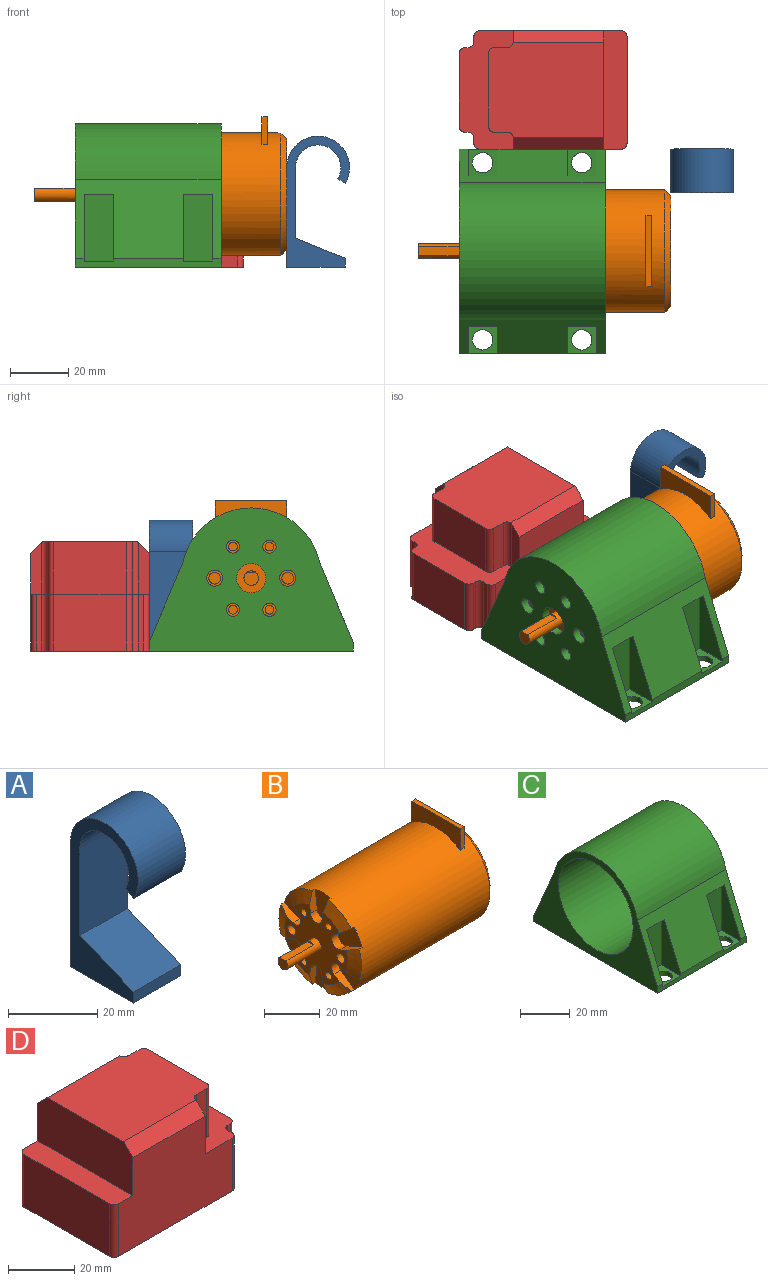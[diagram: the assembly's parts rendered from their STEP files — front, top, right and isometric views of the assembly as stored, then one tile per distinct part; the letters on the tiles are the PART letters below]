
ASSEMBLY  parts=4 mates=11
PART A: 10 faces, bbox 15x21.5x44.9 mm
  f0: cylinder r=7.76mm len=15.53mm, axis (-1,0,0), area 426.9mm2, adj f1,f7,f8,f9
  f1: plane 24.12x15mm, normal (0,-1,0), area 361.8mm2, adj f0,f2,f8,f9
  f2: plane 17x15mm, normal (0,-0.38,0.92), area 275.8mm2, adj f1,f3,f8,f9
  f3: plane 15x3mm, normal (0,-1,0), area 45mm2, adj f2,f4,f8,f9
  f4: plane 20x15mm, normal (0,0,-1), area 300mm2, adj f3,f5,f8,f9
  f5: plane 34.12x15mm, normal (0,1,0), area 511.8mm2, adj f4,f6,f8,f9
  f6: cylinder r=10.76mm len=21.53mm, axis (-1,0,0), area 591.8mm2, adj f5,f7,f8,f9
  f7: plane 15x2.6mm, normal (0,0.5,-0.87), area 45mm2, adj f0,f6,f8,f9
  f8: plane 44.88x21.53mm, normal (1,0,0), area 314.7mm2, adj f0,f1,f2,f3,f4,f5,f6,f7
  f9: plane 44.88x21.53mm, normal (-1,0,0), area 314.7mm2, adj f0,f1,f2,f3,f4,f5,f6,f7
PART B: 55 faces, bbox 86.6x42.1x47.6 mm
  f0: plane 38x38mm, normal (1,0,0), area 1134.1mm2, adj f5
  f1: plane 9.44x2mm, normal (0,-1,0), area 18.9mm2, adj f3,f4,f53,f54
  f2: plane 9.44x2mm, normal (0,1,0), area 18.9mm2, adj f3,f4,f53,f54
  f3: plane 24.5x2mm, normal (0,0,1), area 49mm2, adj f1,f2,f53,f54
  f4: cylinder r=21mm len=65.5mm, axis (-1,0,0), area 8517.7mm2, adj f1,f2,f5,f6,f7,f8,f9,f10
  f5: cone r=19mm half-angle=45deg, axis (-1,0,0), area 355.4mm2, adj f0,f4
  f6: cone r=21mm half-angle=68.2deg, axis (1,0,0), area 64mm2, adj f4,f12,f35,f37
  f7: cone r=21mm half-angle=68.2deg, axis (1,0,0), area 64mm2, adj f4,f12,f31,f33
  f8: cone r=21mm half-angle=68.2deg, axis (1,0,0), area 64mm2, adj f4,f12,f27,f29
  f9: cone r=21mm half-angle=68.2deg, axis (1,0,0), area 64mm2, adj f4,f12,f23,f25
  f10: cone r=21mm half-angle=68.2deg, axis (1,0,0), area 64mm2, adj f4,f12,f19,f21
  f11: cone r=21mm half-angle=68.2deg, axis (1,0,0), area 64mm2, adj f4,f12,f17,f39
  f12: plane 32x31.27mm, normal (-1,0,0), area 515.6mm2, adj f6,f7,f8,f9,f10,f11,f13,f17
  f13: cylinder r=2.5mm len=17mm, axis (1,0,0), area 219.7mm2, adj f12,f14,f15,f16
  f14: plane 5x4.45mm, normal (-1,0,0), area 18.5mm2, adj f13,f15
  f15: plane 14x3.13mm, normal (0,0,1), area 43.8mm2, adj f13,f14,f16
  f16: plane 3.13x0.55mm, normal (-1,0,0), area 1.2mm2, adj f13,f15
  f17: plane 8.53x3.56mm, normal (0,-0.99,0.12), area 24.9mm2, adj f4,f11,f12,f18,f20
  f18: cylinder r=3mm len=5.96mm, axis (-1,0,0), area 30.5mm2, adj f12,f17,f19,f20
  f19: plane 8.53x3.56mm, normal (0,0.99,0.12), area 24.9mm2, adj f4,f10,f12,f18,f20
  f20: plane 11.5x8.01mm, normal (-1,0,0), area 73.2mm2, adj f4,f17,f18,f19
  f21: plane 6.88x5.18mm, normal (0,-0.6,-0.8), area 24.9mm2, adj f4,f10,f12,f22,f24
  f22: cylinder r=3mm len=5.4mm, axis (-1,0,0), area 30.5mm2, adj f12,f21,f23,f24
  f23: plane 7.91x3.56mm, normal (0,0.39,0.92), area 24.9mm2, adj f4,f9,f12,f22,f24
  f24: plane 12.03x10.52mm, normal (-1,0,0), area 73.2mm2, adj f4,f21,f22,f23
  f25: plane 7.91x3.56mm, normal (0,0.39,-0.92), area 24.9mm2, adj f4,f9,f12,f26,f28
  f26: cylinder r=3mm len=5.4mm, axis (-1,0,0), area 30.5mm2, adj f12,f25,f27,f28
  f27: plane 6.88x5.18mm, normal (0,-0.6,0.8), area 24.9mm2, adj f4,f8,f12,f26,f28
  f28: plane 12.03x10.52mm, normal (-1,0,0), area 73.2mm2, adj f4,f25,f26,f27
  f29: plane 8.53x3.56mm, normal (0,0.99,-0.12), area 24.9mm2, adj f4,f8,f12,f30,f32
  f30: cylinder r=3mm len=5.96mm, axis (-1,0,0), area 30.5mm2, adj f12,f29,f31,f32
  f31: plane 8.53x3.56mm, normal (0,-0.99,-0.12), area 24.9mm2, adj f4,f7,f12,f30,f32
  f32: plane 11.5x8.01mm, normal (-1,0,0), area 73.2mm2, adj f4,f29,f30,f31
  f33: plane 6.88x5.18mm, normal (0,0.6,0.8), area 24.9mm2, adj f4,f7,f12,f34,f36
  f34: cylinder r=3mm len=5.4mm, axis (-1,0,0), area 30.5mm2, adj f12,f33,f35,f36
  f35: plane 7.91x3.56mm, normal (0,-0.39,-0.92), area 24.9mm2, adj f4,f6,f12,f34,f36
  f36: plane 12.03x10.52mm, normal (-1,0,0), area 73.2mm2, adj f4,f33,f34,f35
  f37: plane 7.91x3.56mm, normal (0,-0.39,0.92), area 24.9mm2, adj f4,f6,f12,f38,f40
  f38: cylinder r=3mm len=5.4mm, axis (-1,0,0), area 30.5mm2, adj f12,f37,f39,f40
  f39: plane 6.88x5.18mm, normal (0,0.6,-0.8), area 24.9mm2, adj f4,f11,f12,f38,f40
  f40: plane 12.03x10.52mm, normal (-1,0,0), area 73.2mm2, adj f4,f37,f38,f39
  f41: cylinder r=2mm len=10mm, axis (-1,0,0), area 125.7mm2, adj f12,f52
  f42: cylinder r=1.5mm len=10mm, axis (-1,0,0), area 94.2mm2, adj f12,f51
  f43: cylinder r=1.5mm len=10mm, axis (-1,0,0), area 94.2mm2, adj f12,f50
  f44: cylinder r=1.5mm len=10mm, axis (-1,0,0), area 94.2mm2, adj f12,f49
  f45: cylinder r=2mm len=10mm, axis (-1,0,0), area 125.7mm2, adj f12,f48
  f46: cylinder r=1.5mm len=10mm, axis (-1,0,0), area 94.2mm2, adj f12,f47
  f47: plane 3x3mm, normal (-1,0,0), area 7.1mm2, adj f46
  f48: plane 4x4mm, normal (-1,0,0), area 12.6mm2, adj f45
  f49: plane 3x3mm, normal (-1,0,0), area 7.1mm2, adj f44
  f50: plane 3x3mm, normal (-1,0,0), area 7.1mm2, adj f43
  f51: plane 3x3mm, normal (-1,0,0), area 7.1mm2, adj f42
  f52: plane 4x4mm, normal (-1,0,0), area 12.6mm2, adj f41
  f53: plane 24.5x9.44mm, normal (-1,0,0), area 165.6mm2, adj f1,f2,f3,f4
  f54: plane 24.5x9.44mm, normal (1,0,0), area 165.6mm2, adj f1,f2,f3,f4
PART C: 41 faces, bbox 50x70x49.1 mm
  f0: plane 50x27mm, normal (0,-0.92,0.39), area 988.1mm2, adj f1,f10,f13,f14,f22,f23,f26,f32
  f1: plane 50x3mm, normal (0,-1,0), area 130mm2, adj f0,f10,f14,f15,f22,f23,f25,f32
  f2: plane 50x3mm, normal (0,1,0), area 130mm2, adj f10,f14,f15,f16,f17,f19,f20,f27
  f3: cylinder r=5mm len=10mm, axis (-1,0,0), area 94.2mm2, adj f10,f11
  f4: cylinder r=2.25mm len=4.5mm, axis (-1,0,0), area 42.4mm2, adj f10,f11
  f5: cylinder r=2.25mm len=4.5mm, axis (-1,0,0), area 42.4mm2, adj f10,f11
  f6: cylinder r=2.25mm len=4.5mm, axis (-1,0,0), area 42.4mm2, adj f10,f11
  f7: cylinder r=2.25mm len=4.5mm, axis (-1,0,0), area 42.4mm2, adj f10,f11
  f8: cylinder r=2.75mm len=5.5mm, axis (-1,0,0), area 51.8mm2, adj f10,f11
  f9: cylinder r=2.75mm len=5.5mm, axis (-1,0,0), area 51.8mm2, adj f10,f11
  f10: plane 70x49.1mm, normal (1,0,0), area 2274.9mm2, adj f0,f1,f2,f3,f4,f5,f6,f7
  f11: plane 42.2x42.2mm, normal (-1,0,0), area 1209mm2, adj f3,f4,f5,f6,f7,f8,f9,f12
  f12: cylinder r=21.1mm len=47mm, axis (1,0,0), area 6231mm2, adj f11,f14
  f13: cylinder r=24.1mm len=50mm, axis (1,0,0), area 3282mm2, adj f0,f10,f14,f16
  f14: plane 70x49.1mm, normal (-1,0,0), area 1065.9mm2, adj f0,f1,f2,f12,f13,f15,f16
  f15: plane 70x50mm, normal (0,0,-1), area 3346.1mm2, adj f1,f2,f10,f14,f37,f38,f39,f40
  f16: plane 50x27mm, normal (0,0.92,0.39), area 988.1mm2, adj f2,f10,f13,f14,f17,f19,f21,f27
  f17: plane 23x11mm, normal (1,0,0), area 150.6mm2, adj f2,f16,f18,f20,f21
  f18: plane 23x10mm, normal (0,1,0), area 230mm2, adj f17,f19,f20,f21
  f19: plane 23x11mm, normal (-1,0,0), area 150.6mm2, adj f2,f16,f18,f20,f21
  f20: plane 11x10mm, normal (0,0,1), area 71.5mm2, adj f2,f17,f18,f19,f40
  f21: plane 10x1.69mm, normal (0,0,-1), area 16.9mm2, adj f16,f17,f18,f19
  f22: plane 23x11mm, normal (1,0,0), area 150.6mm2, adj f0,f1,f24,f25,f26
  f23: plane 23x11mm, normal (-1,0,0), area 150.6mm2, adj f0,f1,f24,f25,f26
  f24: plane 23x10mm, normal (0,-1,0), area 230mm2, adj f22,f23,f25,f26
  f25: plane 11x10mm, normal (0,0,1), area 71.5mm2, adj f1,f22,f23,f24,f39
  f26: plane 10x1.69mm, normal (0,0,-1), area 16.9mm2, adj f0,f22,f23,f24
  f27: plane 23x11mm, normal (1,0,0), area 150.6mm2, adj f2,f16,f28,f30,f31
  f28: plane 23x10mm, normal (0,1,0), area 230mm2, adj f27,f29,f30,f31
  f29: plane 23x11mm, normal (-1,0,0), area 150.6mm2, adj f2,f16,f28,f30,f31
  f30: plane 11x10mm, normal (0,0,1), area 71.5mm2, adj f2,f27,f28,f29,f38
  f31: plane 10x1.69mm, normal (0,0,-1), area 16.9mm2, adj f16,f27,f28,f29
  f32: plane 23x11mm, normal (1,0,0), area 150.6mm2, adj f0,f1,f34,f35,f36
  f33: plane 23x11mm, normal (-1,0,0), area 150.6mm2, adj f0,f1,f34,f35,f36
  f34: plane 23x10mm, normal (0,-1,0), area 230mm2, adj f32,f33,f35,f36
  f35: plane 11x10mm, normal (0,0,1), area 71.5mm2, adj f1,f32,f33,f34,f37
  f36: plane 10x1.69mm, normal (0,0,-1), area 16.9mm2, adj f0,f32,f33,f34
  f37: cylinder r=3.5mm len=7mm, axis (0,0,1), area 44mm2, adj f15,f35
  f38: cylinder r=3.5mm len=7mm, axis (0,0,1), area 44mm2, adj f15,f30
  f39: cylinder r=3.5mm len=7mm, axis (0,0,1), area 44mm2, adj f15,f25
  f40: cylinder r=3.5mm len=7mm, axis (0,0,1), area 44mm2, adj f15,f20
PART D: 32 faces, bbox 57.5x40.6x37.5 mm
  f0: plane 40.6x18.5mm, normal (0,0,1), area 444.9mm2, adj f1,f2,f4,f5,f6,f7,f8,f12
  f1: plane 19.5x1.8mm, normal (1,0,0), area 35.1mm2, adj f0,f10,f24,f31
  f2: plane 48.5x33.5mm, normal (0,1,0), area 1379.7mm2, adj f0,f9,f10,f11,f16,f18,f24,f25
  f3: plane 36.6x19.5mm, normal (-1,0,0), area 713.7mm2, adj f9,f10,f25,f26
  f4: plane 48.5x33.5mm, normal (0,-1,0), area 1379.7mm2, adj f0,f9,f10,f11,f12,f19,f26,f27
  f5: plane 19.5x1.8mm, normal (1,0,0), area 35.1mm2, adj f0,f10,f27,f28
  f6: plane 19.5x1mm, normal (0,-1,0), area 19.5mm2, adj f0,f10,f28,f29
  f7: plane 25x19.5mm, normal (1,0,0), area 487.5mm2, adj f0,f10,f29,f30
  f8: plane 19.5x1mm, normal (0,1,0), area 19.5mm2, adj f0,f10,f30,f31
  f9: plane 40.6x8mm, normal (0,0,1), area 323.1mm2, adj f2,f3,f4,f11,f25,f26
  f10: plane 57.5x40.6mm, normal (0,0,-1), area 2273.1mm2, adj f1,f2,f3,f4,f5,f6,f7,f8
  f11: plane 40.6x18mm, normal (-1,0,0), area 714.8mm2, adj f2,f4,f9,f17,f18,f19
  f12: plane 17.8x3.8mm, normal (1,0,0), area 60.4mm2, adj f0,f4,f19,f20
  f13: plane 18x4.5mm, normal (0,-1,0), area 81mm2, adj f0,f17,f20,f21
  f14: plane 25x18mm, normal (1,0,0), area 450mm2, adj f0,f17,f21,f22
  f15: plane 18x4.5mm, normal (0,1,0), area 81mm2, adj f0,f17,f22,f23
  f16: plane 17.8x3.8mm, normal (1,0,0), area 60.4mm2, adj f0,f2,f18,f23
  f17: plane 39.5x32.6mm, normal (0,0,1), area 1257.1mm2, adj f11,f13,f14,f15,f18,f19,f20,f21
  f18: plane 31.01x4mm, normal (0,0.71,0.71), area 175.4mm2, adj f2,f11,f16,f17,f23
  f19: plane 31.01x4mm, normal (0,-0.71,0.71), area 175.4mm2, adj f4,f11,f12,f17,f20
  f20: cylinder r=2mm len=18mm, axis (0,0,-1), area 56.5mm2, adj f0,f12,f13,f17,f19
  f21: cylinder r=2mm len=18mm, axis (0,0,1), area 56.5mm2, adj f0,f13,f14,f17
  f22: cylinder r=2mm len=18mm, axis (0,0,-1), area 56.5mm2, adj f0,f14,f15,f17
  f23: cylinder r=2mm len=18mm, axis (0,0,1), area 56.5mm2, adj f0,f15,f16,f17,f18
  f24: cylinder r=2mm len=19.5mm, axis (0,0,1), area 61.3mm2, adj f0,f1,f2,f10
  f25: cylinder r=2mm len=19.5mm, axis (0,0,-1), area 61.3mm2, adj f2,f3,f9,f10
  f26: cylinder r=2mm len=19.5mm, axis (0,0,1), area 61.3mm2, adj f3,f4,f9,f10
  f27: cylinder r=2mm len=19.5mm, axis (0,0,-1), area 61.3mm2, adj f0,f4,f5,f10
  f28: cylinder r=2mm len=19.5mm, axis (0,0,-1), area 61.3mm2, adj f0,f5,f6,f10
  f29: cylinder r=2mm len=19.5mm, axis (0,0,1), area 61.3mm2, adj f0,f6,f7,f10
  f30: cylinder r=2mm len=19.5mm, axis (0,0,-1), area 61.3mm2, adj f0,f7,f8,f10
  f31: cylinder r=2mm len=19.5mm, axis (0,0,1), area 61.3mm2, adj f0,f1,f8,f10
PLACE A rot(axis=(0,0,1),90deg) t=(69.5,20,-25)mm
PLACE B at identity fixed
PLACE C rot(axis=(0,0,1),180deg) t=(0,0,0)mm
PLACE D rot(axis=(0,0,1),180deg) t=(28.25,55.3,-25)mm
MATE planar A.f8 <-> D.f2  axis (0,1,0) through (69.5,35,-25)mm
MATE parallel D.f3 <-> C.f10  axis (1,0,0) through (54.5,37,-15.25)mm
MATE parallel A.f5 <-> C.f14  axis (-1,0,0) through (69.5,27.5,-7.94)mm
MATE planar A.f4 <-> C.f15  axis (0,0,-1) through (79.5,27.5,-25)mm
MATE planar D.f10 <-> C.f15  axis (0,0,-1) through (26.42,55.3,-25)mm
MATE planar D.f7 <-> C.f10  axis (-1,0,0) through (-3,55.3,-15.25)mm
MATE parallel C.f15 <-> B.f3  axis (0,0,-1) through (22,0,-25)mm
MATE planar C.f13 <-> B.f4  axis (1,0,0) through (0,0,0)mm
MATE planar D.f2 <-> C.f1  axis (0,-1,0) through (29.12,35,-9.98)mm
MATE planar A.f5 <-> B.f4  axis (-1,0,0) through (69.5,27.5,-7.94)mm
MATE cylindrical C.f12 <-> B.f4  axis (-1,0,0) through (23.5,0,0)mm
